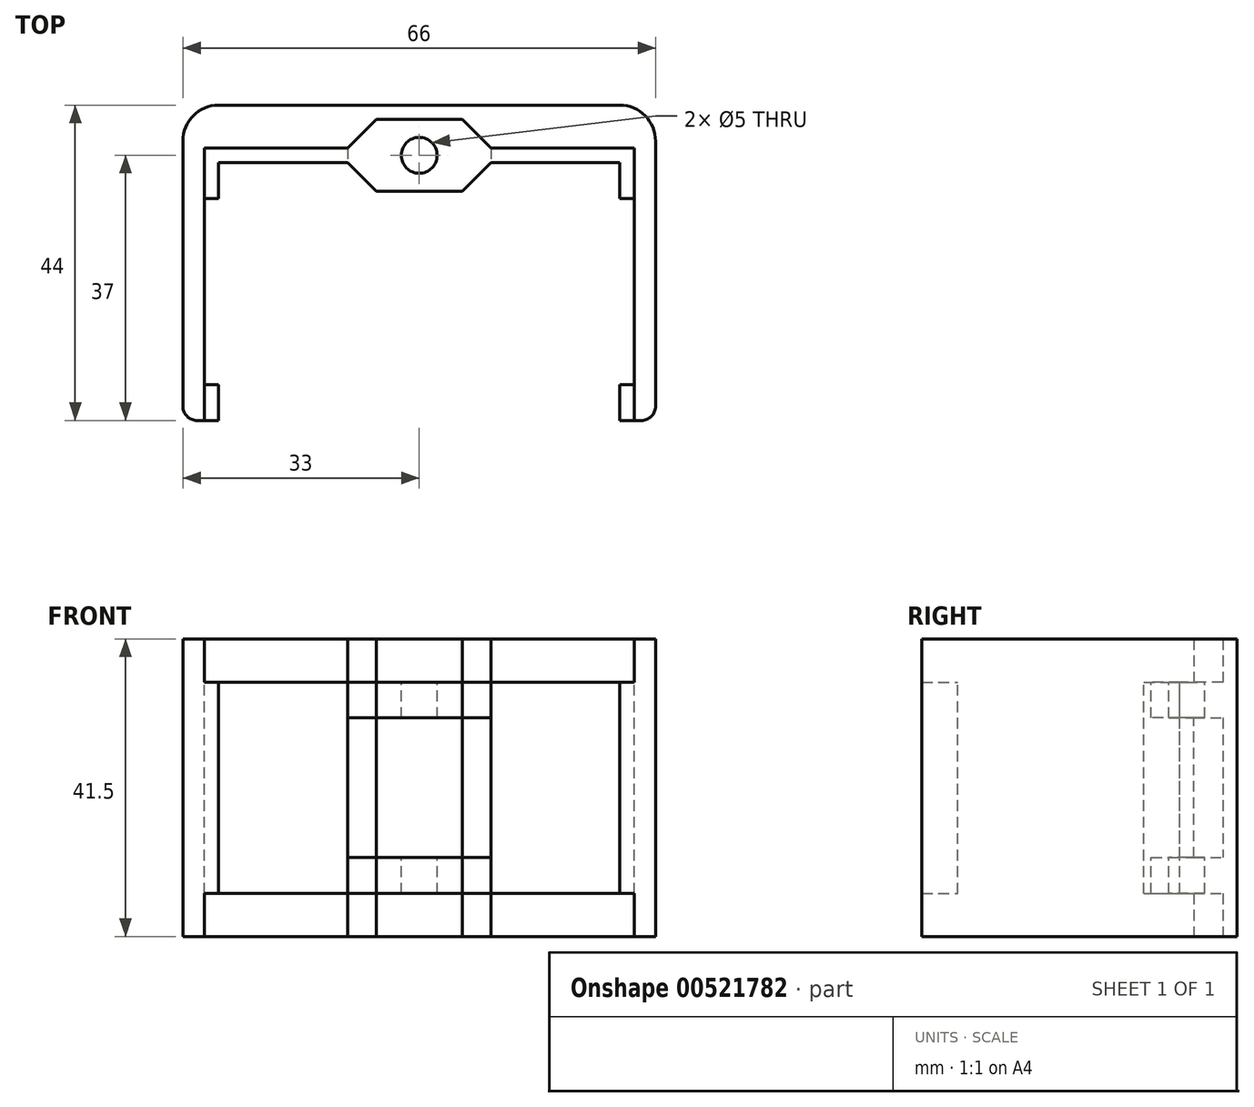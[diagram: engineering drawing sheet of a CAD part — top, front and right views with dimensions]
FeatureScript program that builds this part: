
annotation { "Feature Type Name" : "Feature", "Feature Type Description" : "" }
export const myFeature = defineFeature(function(context is Context, id is Id, definition is map)
    precondition{}
    {
        {
            var Q0;
            Q0=qCreatedBy(makeId("Top.planeOp"),FACE);
            var sketch = newSketch(context, id + "F0", { "sketchPlane" : qUnion([Q0])});
            skLineSegment(sketch, "E0.bottom", {"start": v(30, -19) * mm, "end": v(-30, -19) * mm});
            skLineSegment(sketch, "E0.top", {"start": v(30, 19) * mm, "end": v(10, 19) * mm});
            skLineSegment(sketch, "E0.left", {"start": v(30, -19) * mm, "end": v(30, 19) * mm});
            skLineSegment(sketch, "E0.right", {"start": v(-30, -19) * mm, "end": v(-30, 19) * mm});
            skPoint(sketch, "E0.middle", {"position": v(0, 0) * mm});
            skPoint(sketch, "E1", {"position": v(-10, 19) * mm});
            skPoint(sketch, "E2", {"position": v(10, 19) * mm});
            skPoint(sketch, "E3", {"position": v(0, 23) * mm});
            skPoint(sketch, "E3.positionSnap0", {"position": v(0, 19) * mm});
            skPoint(sketch, "E4", {"position": v(-6, 23) * mm});
            skPoint(sketch, "E5", {"position": v(6, 23) * mm});
            skLineSegment(sketch, "E6", {"start": v(-10, 19) * mm, "end": v(-6, 23) * mm});
            skLineSegment(sketch, "E7", {"start": v(-6, 23) * mm, "end": v(6, 23) * mm});
            skLineSegment(sketch, "E8", {"start": v(6, 23) * mm, "end": v(10, 19) * mm});
            skLineSegment(sketch, "E9.trimOffspring", {"start": v(-10, 19) * mm, "end": v(-30, 19) * mm});
            skLineSegment(sketch, "E10", {"start": v(-10, 19) * mm, "end": v(10, 19) * mm});
            skLineSegment(sketch, "E11.0", {"start": v(-33, -19) * mm, "end": v(-33, 19) * mm});
            skLineSegment(sketch, "E12.0", {"start": v(33, -19) * mm, "end": v(33, 19) * mm});
            skLineSegment(sketch, "E13", {"start": v(-33, 19) * mm, "end": v(-33, 20) * mm});
            skLineSegment(sketch, "E14", {"start": v(33, 20) * mm, "end": v(33, 19) * mm});
            skLineSegment(sketch, "E15", {"start": v(-33, -19) * mm, "end": v(-30, -19) * mm});
            skLineSegment(sketch, "E16", {"start": v(33, -19) * mm, "end": v(30, -19) * mm});
            skLineSegment(sketch, "E17", {"start": v(-28, 25) * mm, "end": v(28, 25) * mm});
            skPoint(sketch, "E18.visualSharp", {"position": v(-33, 25) * mm});
            skArc(sketch, "E18.filletArc", {"start": v(-28, 25) * mm, "mid": v(-31.54, 23.54) * mm, "end": v(-33, 20) * mm});
            skPoint(sketch, "E19.visualSharp", {"position": v(33, 25) * mm});
            skArc(sketch, "E19.filletArc", {"start": v(33, 20) * mm, "mid": v(31.54, 23.54) * mm, "end": v(28, 25) * mm});
            skSolve(sketch);
        }
        {
            var Q0;
            Q0=makeQuery(id+"F0.imprint","IMPRINT",FACE,{"disambiguationData":[TD([[makeQuery(id+"F0.imprint","IMPRINT",EDGE,{"derivedFrom":sQuery(id+"F0.wireOp",EDGE,"E0.top")}),-1.0]])]});
            extrude(context, id + "F1", {"entities" : qUnion([Q0]), "depth" : 41.5 * mm, "offsetDistance" : 25 * mm});
        }
        {
            var Q0;
            Q0=makeQuery(id+"F0.imprint","IMPRINT",FACE,{"disambiguationData":[TD([[makeQuery(id+"F0.imprint","IMPRINT",EDGE,{"derivedFrom":sQuery(id+"F0.wireOp",EDGE,"E0.bottom")}),-1.0]])]});
            var Q1;
            Q1=makeQuery(id+"F0.imprint","IMPRINT",FACE,{"disambiguationData":[TD([[makeQuery(id+"F0.imprint","IMPRINT",EDGE,{"derivedFrom":sQuery(id+"F0.wireOp",EDGE,"E6")}),-1.0]])]});
            extrude(context, id + "F2", {"entities" : qUnion([Q0, Q1]), "operationType" : NewBodyOperationType.ADD, "depth" : 35.5 * mm, "offsetDistance" : 25 * mm});
        }
        {
            var Q0;
            Q0=makeQuery(id+"F0.imprint","IMPRINT",FACE,{"disambiguationData":[TD([[makeQuery(id+"F0.imprint","IMPRINT",EDGE,{"derivedFrom":sQuery(id+"F0.wireOp",EDGE,"E0.bottom")}),-1.0]])]});
            var Q1;
            Q1=makeQuery(id+"F0.imprint","IMPRINT",FACE,{"disambiguationData":[TD([[makeQuery(id+"F0.imprint","IMPRINT",EDGE,{"derivedFrom":sQuery(id+"F0.wireOp",EDGE,"E6")}),-1.0]])]});
            extrude(context, id + "F3", {"entities" : qUnion([Q0, Q1]), "operationType" : NewBodyOperationType.REMOVE, "depth" : 6 * mm, "offsetDistance" : 25 * mm});
        }
        {
            var Q0;
            Q0=makeQuery(id+"F2.opExtrude","CAP_FACE",FACE,{"disambiguationData":[OSD([sQuery(id+"F0.wireOp",EDGE,"E0.bottom"),sQuery(id+"F0.wireOp",EDGE,"E0.top"),sQuery(id+"F0.wireOp",EDGE,"E0.left"),sQuery(id+"F0.wireOp",EDGE,"E0.right"),sQuery(id+"F0.wireOp",EDGE,"E6"),sQuery(id+"F0.wireOp",EDGE,"E7"),sQuery(id+"F0.wireOp",EDGE,"E8"),sQuery(id+"F0.wireOp",EDGE,"E9.trimOffspring")])],"isStart":false});
            var sketch = newSketch(context, id + "F4", { "sketchPlane" : qUnion([Q0])});
            skLineSegment(sketch, "E20.0", {"start": v(-6, 13) * mm, "end": v(6, 13) * mm});
            skLineSegment(sketch, "E21.0", {"start": v(-28, -19) * mm, "end": v(-28, -14) * mm});
            skLineSegment(sketch, "E22.0", {"start": v(-10, 17) * mm, "end": v(-28, 17) * mm});
            skLineSegment(sketch, "E23.0", {"start": v(28, 17) * mm, "end": v(10, 17) * mm});
            skLineSegment(sketch, "E24.0", {"start": v(28, -19) * mm, "end": v(28, -14) * mm});
            skLineSegment(sketch, "E25", {"start": v(-10, 17) * mm, "end": v(-6, 13) * mm});
            skLineSegment(sketch, "E26", {"start": v(6, 13) * mm, "end": v(10, 17) * mm});
            skPoint(sketch, "E27", {"position": v(-28, 17) * mm});
            skPoint(sketch, "E28", {"position": v(28, 17) * mm});
            skPoint(sketch, "E29", {"position": v(-28, 12) * mm});
            skPoint(sketch, "E30", {"position": v(28, 12) * mm});
            skPoint(sketch, "E31", {"position": v(-28, -14) * mm});
            skPoint(sketch, "E32", {"position": v(28, -14) * mm});
            skLineSegment(sketch, "E33", {"start": v(-28, 12) * mm, "end": v(-30, 12) * mm});
            skLineSegment(sketch, "E34", {"start": v(-28, -14) * mm, "end": v(-30, -14) * mm});
            skLineSegment(sketch, "E35", {"start": v(28, 12) * mm, "end": v(30, 12) * mm});
            skLineSegment(sketch, "E36", {"start": v(28, -14) * mm, "end": v(30, -14) * mm});
            skLineSegment(sketch, "E37.trimOffspring", {"start": v(-28, 12) * mm, "end": v(-28, 17) * mm});
            skLineSegment(sketch, "E38.trimOffspring", {"start": v(28, 12) * mm, "end": v(28, 17) * mm});
            skSolve(sketch);
        }
        {
            var Q0;
            Q0=makeQuery(id+"F4.imprint","IMPRINT",FACE,{"disambiguationData":[TD([[makeQuery(id+"F4.imprint","IMPRINT",EDGE,{"derivedFrom":sQuery(id+"F4.wireOp",EDGE,"E20.0")}),-1.0]])]});
            extrude(context, id + "F5", {"entities" : qUnion([Q0]), "operationType" : NewBodyOperationType.REMOVE, "oppositeDirection" : true, "depth" : 50 * mm, "offsetDistance" : 25 * mm});
        }
        {
            var Q0;
            {var subQ0=sQuery(id+"F0.wireOp",EDGE,"E0.right");var subQ1=sQuery(id+"F0.wireOp",EDGE,"E9.trimOffspring");var subQ2=sQuery(id+"F0.wireOp",EDGE,"E0.left");var subQ3=sQuery(id+"F0.wireOp",EDGE,"E8");var subQ4=sQuery(id+"F0.wireOp",EDGE,"E7");var subQ5=sQuery(id+"F0.wireOp",EDGE,"E0.top");var subQ6=sQuery(id+"F0.wireOp",EDGE,"E6");Q0=makeQuery(id+"F5.boolean.opBoolean","SPLIT",FACE,{"disambiguationData":[TD([makeQuery(id+"F1.opExtrude","SWEPT_FACE",FACE,{"disambiguationData":[OSD([subQ5])]})])],"derivedFrom":makeQuery(id+"F2.opExtrude","CAP_FACE",FACE,{"disambiguationData":[OSD([sQuery(id+"F0.wireOp",EDGE,"E0.bottom"),subQ5,subQ2,subQ0,subQ6,subQ4,subQ3,subQ1])],"isStart":false})});}
            var sketch = newSketch(context, id + "F6", { "sketchPlane" : qUnion([Q0])});
            skLineSegment(sketch, "E39", {"start": v(-10, 19) * mm, "end": v(-10, 17) * mm});
            skLineSegment(sketch, "E40", {"start": v(10, 19) * mm, "end": v(10, 17) * mm});
            skPoint(sketch, "E41", {"position": v(0, 18) * mm});
            skPoint(sketch, "E41.positionSnap0", {"position": v(0, 23) * mm});
            skCircle(sketch, "E42", {"center": v(0, 18) * mm, "radius": 2.5 * mm});
            skSolve(sketch);
        }
        {
            var Q0;
            Q0=makeQuery(id+"F6.imprint","IMPRINT",FACE,{"disambiguationData":[TD([[makeQuery(id+"F6.imprint","IMPRINT",EDGE,{"derivedFrom":sQuery(id+"F6.wireOp",EDGE,"E39")}),1.0]])]});
            extrude(context, id + "F7", {"entities" : qUnion([Q0]), "operationType" : NewBodyOperationType.REMOVE, "oppositeDirection" : true, "depth" : 5 * mm, "offsetDistance" : 25 * mm});
        }
        {
            var Q0;
            Q0=makeQuery(id+"F7.boolean.opBoolean","COPY",FACE,{"derivedFrom":makeQuery(id+"F7.opExtrude","CAP_FACE",FACE,{"disambiguationData":[OSD([sQuery(id+"F0.wireOp",EDGE,"E6"),sQuery(id+"F0.wireOp",EDGE,"E7"),sQuery(id+"F0.wireOp",EDGE,"E8"),sQuery(id+"F4.wireOp",EDGE,"E20.0"),sQuery(id+"F4.wireOp",EDGE,"E25"),sQuery(id+"F4.wireOp",EDGE,"E26"),sQuery(id+"F6.wireOp",EDGE,"E39"),sQuery(id+"F6.wireOp",EDGE,"E40")])],"isStart":false})});
            extrude(context, id + "F8", {"entities" : qUnion([Q0]), "operationType" : NewBodyOperationType.REMOVE, "oppositeDirection" : true, "depth" : 19.5 * mm, "offsetDistance" : 25 * mm});
        }
        {
            var Q0;
            Q0=makeQuery(id+"F6.imprint","IMPRINT",FACE,{"disambiguationData":[TD([[makeQuery(id+"F6.imprint","IMPRINT",EDGE,{"derivedFrom":sQuery(id+"F6.wireOp",EDGE,"E39")}),1.0]])]});
            extrude(context, id + "F9", {"entities" : qUnion([Q0]), "operationType" : NewBodyOperationType.ADD, "oppositeDirection" : true, "depth" : 5 * mm, "offsetDistance" : 25 * mm});
        }
        {
            var Q0;
            Q0=makeQuery(id+"F6.imprint","IMPRINT",FACE,{"disambiguationData":[TD([[makeQuery(id+"F6.imprint","IMPRINT",EDGE,{"derivedFrom":sQuery(id+"F6.wireOp",EDGE,"E42")}),1.0]])]});
            extrude(context, id + "F10", {"entities" : qUnion([Q0]), "operationType" : NewBodyOperationType.REMOVE, "oppositeDirection" : true, "depth" : 50 * mm, "offsetDistance" : 25 * mm});
        }
        {
            var Q0;
            Q0=makeQuery(id+"F1.opExtrude","SWEPT_EDGE",EDGE,{"disambiguationData":[OSD([sQuery(id+"F0.wireOp",EDGE,"E11.0"),sQuery(id+"F0.wireOp",EDGE,"E15")])]});
            var Q1;
            Q1=makeQuery(id+"F1.opExtrude","SWEPT_EDGE",EDGE,{"disambiguationData":[OSD([sQuery(id+"F0.wireOp",EDGE,"E12.0"),sQuery(id+"F0.wireOp",EDGE,"E16")])]});
            fillet(context, id + "F11", {"entities" : qUnion([Q0, Q1]), "tangentPropagation" : true, "radius" : 2 * mm, "defaultsChanged" : true, "vertexSettings" : [], "allowEdgeOverflow" : false});
        }
    });
